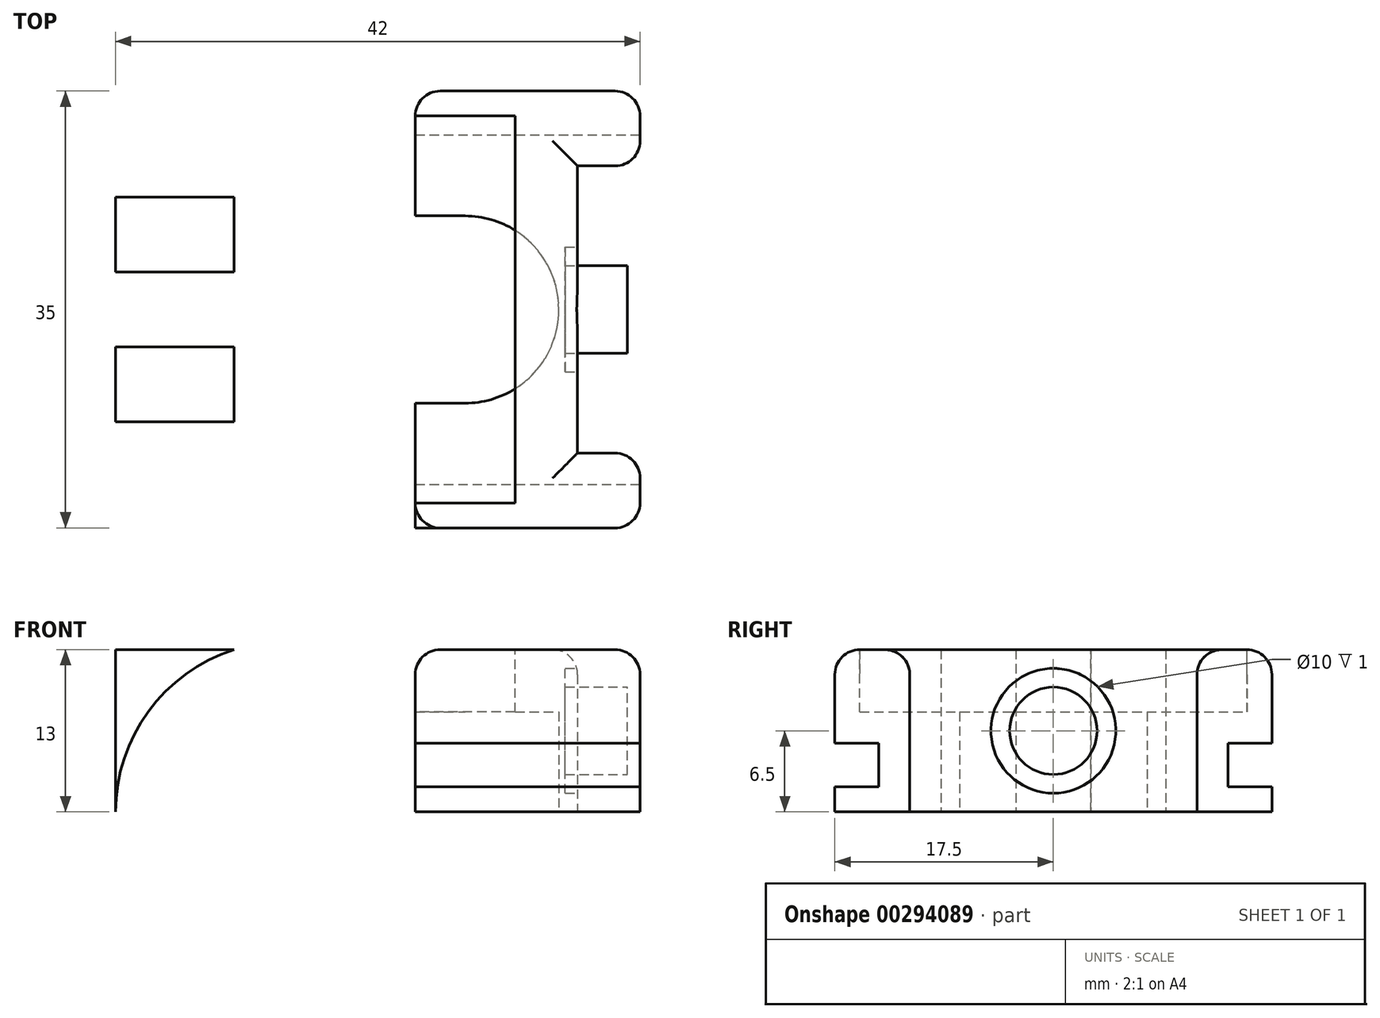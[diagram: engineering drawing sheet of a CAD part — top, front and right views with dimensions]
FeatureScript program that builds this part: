
annotation { "Feature Type Name" : "Feature", "Feature Type Description" : "" }
export const myFeature = defineFeature(function(context is Context, id is Id, definition is map)
    precondition{}
    {
        {
            var Q0;
            Q0=qCreatedBy(makeId("Top.planeOp"),FACE);
            var sketch = newSketch(context, id + "F0", { "sketchPlane" : qUnion([Q0])});
            skLineSegment(sketch, "E0", {"start": v(-15.8, 20.5) * mm, "end": v(2.2, 20.5) * mm});
            skLineSegment(sketch, "E1", {"start": v(2.2, 20.5) * mm, "end": v(2.2, 14.5) * mm});
            skLineSegment(sketch, "E2", {"start": v(2.2, 14.5) * mm, "end": v(-2.8, 14.5) * mm});
            skLineSegment(sketch, "E3", {"start": v(-2.8, 14.5) * mm, "end": v(-2.8, -8.5) * mm});
            skLineSegment(sketch, "E4", {"start": v(-2.8, -8.5) * mm, "end": v(2.2, -8.5) * mm});
            skPoint(sketch, "E4.endSnap0", {"position": v(2.2, 17.5) * mm});
            skLineSegment(sketch, "E5", {"start": v(2.2, -8.5) * mm, "end": v(2.2, -14.5) * mm});
            skLineSegment(sketch, "E6", {"start": v(2.2, -14.5) * mm, "end": v(-15.8, -14.5) * mm});
            skLineSegment(sketch, "E7", {"start": v(-15.8, -14.5) * mm, "end": v(-15.8, -6) * mm});
            skLineSegment(sketch, "E8", {"start": v(-15.8, 20.5) * mm, "end": v(-15.8, 12) * mm});
            skLineSegment(sketch, "E9", {"start": v(-15.8, 12) * mm, "end": v(-39.8, 12) * mm});
            skLineSegment(sketch, "E10", {"start": v(-15.8, -6) * mm, "end": v(-39.8, -6) * mm});
            skLineSegment(sketch, "E11", {"start": v(-39.8, -6) * mm, "end": v(-39.8, 0) * mm});
            skLineSegment(sketch, "E12", {"start": v(-39.8, 12) * mm, "end": v(-39.8, 6) * mm});
            skLineSegment(sketch, "E13", {"start": v(-39.8, 6) * mm, "end": v(-28.8, 6) * mm});
            skLineSegment(sketch, "E14", {"start": v(-28.8, 6) * mm, "end": v(-28.8, 0) * mm});
            skLineSegment(sketch, "E15", {"start": v(-28.8, 0) * mm, "end": v(-39.8, 0) * mm});
            skPoint(sketch, "E16.startSnap0", {"position": v(-28.8, 3) * mm});
            skLineSegment(sketch, "E17", {"start": v(-29.8, 12) * mm, "end": v(-29.8, -6) * mm});
            skSolve(sketch);
        }
        {
            var Q0;
            {var subQ0=sQuery(id+"F0.wireOp",EDGE,"E12");Q0=makeQuery(id+"F0.imprint","IMPRINT",FACE,{"disambiguationData":[TD([[makeQuery(id+"F0.imprint","IMPRINT",EDGE,{"derivedFrom":subQ0}),1.0]])]});}
            var Q1;
            {var subQ0=sQuery(id+"F0.wireOp",EDGE,"E11");Q1=makeQuery(id+"F0.imprint","IMPRINT",FACE,{"disambiguationData":[TD([[makeQuery(id+"F0.imprint","IMPRINT",EDGE,{"derivedFrom":subQ0}),-1.0]])]});}
            var Q2;
            Q2=makeQuery(id+"F0.imprint","IMPRINT",FACE,{"disambiguationData":[TD([[makeQuery(id+"F0.imprint","IMPRINT",EDGE,{"derivedFrom":sQuery(id+"F0.wireOp",EDGE,"E0")}),-1.0]])]});
            extrude(context, id + "F1", {"entities" : qUnion([Q0, Q1, Q2]), "depth" : 13 * mm});
        }
        {
            var Q0;
            Q0=makeQuery(id+"F1.opExtrude","SWEPT_FACE",FACE,{"disambiguationData":[OSD([sQuery(id+"F0.wireOp",EDGE,"E10")])]});
            var sketch = newSketch(context, id + "F2", { "sketchPlane" : qUnion([Q0])});
            skPoint(sketch, "E18", {"position": v(-26.15, 0) * mm});
            skArc(sketch, "E19", {"start": v(-39.8, 0) * mm, "mid": v(-37.18, 8.04) * mm, "end": v(-30.33, 13) * mm});
            skSolve(sketch);
        }
        {
            var Q0;
            {var subQ0=sQuery(id+"F2.wireOp",EDGE,"E19");Q0=makeQuery(id+"F2.imprint","IMPRINT",FACE,{"disambiguationData":[TD([[makeQuery(id+"F2.imprint","IMPRINT",EDGE,{"derivedFrom":subQ0}),1.0]])]});}
            extrude(context, id + "F3", {"entities" : qUnion([Q0]), "operationType" : NewBodyOperationType.REMOVE, "oppositeDirection" : true, "depth" : 25 * mm});
        }
        {
            var Q0;
            Q0=makeQuery(id+"F1.opExtrude","CAP_FACE",FACE,{"disambiguationData":[OSD([sQuery(id+"F0.wireOp",EDGE,"E0"),sQuery(id+"F0.wireOp",EDGE,"E1"),sQuery(id+"F0.wireOp",EDGE,"E2"),sQuery(id+"F0.wireOp",EDGE,"E3"),sQuery(id+"F0.wireOp",EDGE,"E4"),sQuery(id+"F0.wireOp",EDGE,"E5"),sQuery(id+"F0.wireOp",EDGE,"E6"),sQuery(id+"F0.wireOp",EDGE,"E7"),sQuery(id+"F0.wireOp",EDGE,"E8"),sQuery(id+"F0.wireOp",EDGE,"E9"),sQuery(id+"F0.wireOp",EDGE,"E10"),sQuery(id+"F0.wireOp",EDGE,"E11"),sQuery(id+"F0.wireOp",EDGE,"E12"),sQuery(id+"F0.wireOp",EDGE,"E13"),sQuery(id+"F0.wireOp",EDGE,"E14"),sQuery(id+"F0.wireOp",EDGE,"E15")])],"isStart":false});
            var sketch = newSketch(context, id + "F4", { "sketchPlane" : qUnion([Q0])});
            skLineSegment(sketch, "E20", {"start": v(-7.8, 18.5) * mm, "end": v(-30.33, 18.5) * mm});
            skLineSegment(sketch, "E21", {"start": v(-30.33, 18.5) * mm, "end": v(-30.33, -12.5) * mm});
            skLineSegment(sketch, "E22", {"start": v(-30.33, -12.5) * mm, "end": v(-7.8, -12.5) * mm});
            skLineSegment(sketch, "E23", {"start": v(-7.8, -12.5) * mm, "end": v(-7.8, 18.5) * mm});
            skSolve(sketch);
        }
        {
            var Q0;
            Q0 = qSketchRegion(id + "F4", true);
            extrude(context, id + "F5", {"entities" : qUnion([Q0]), "operationType" : NewBodyOperationType.REMOVE, "oppositeDirection" : true, "depth" : 5 * mm});
        }
        {
            var Q0;
            Q0=makeQuery(id+"F1.opExtrude","CAP_FACE",FACE,{"disambiguationData":[OSD([sQuery(id+"F0.wireOp",EDGE,"E0"),sQuery(id+"F0.wireOp",EDGE,"E1"),sQuery(id+"F0.wireOp",EDGE,"E2"),sQuery(id+"F0.wireOp",EDGE,"E3"),sQuery(id+"F0.wireOp",EDGE,"E4"),sQuery(id+"F0.wireOp",EDGE,"E5"),sQuery(id+"F0.wireOp",EDGE,"E6"),sQuery(id+"F0.wireOp",EDGE,"E7"),sQuery(id+"F0.wireOp",EDGE,"E8"),sQuery(id+"F0.wireOp",EDGE,"E9"),sQuery(id+"F0.wireOp",EDGE,"E10"),sQuery(id+"F0.wireOp",EDGE,"E11"),sQuery(id+"F0.wireOp",EDGE,"E12"),sQuery(id+"F0.wireOp",EDGE,"E13"),sQuery(id+"F0.wireOp",EDGE,"E14"),sQuery(id+"F0.wireOp",EDGE,"E15")])],"isStart":true});
            var sketch = newSketch(context, id + "F6", { "sketchPlane" : qUnion([Q0])});
            skLineSegment(sketch, "E24", {"start": v(-28.8, -3) * mm, "end": v(-2.8, -3) * mm, "construction": true});
            skLineSegment(sketch, "E25", {"start": v(-27.8, 4.5) * mm, "end": v(-3.53, 4.5) * mm, "construction": true});
            skPoint(sketch, "E26", {"position": v(-20.3, -3) * mm});
            skArc(sketch, "E27", {"start": v(-20.3, 4.5) * mm, "mid": v(-27.8, -3) * mm, "end": v(-20.3, -10.5) * mm});
            skPoint(sketch, "E28", {"position": v(-11.8, -3) * mm});
            skArc(sketch, "E29", {"start": v(-11.8, 4.5) * mm, "mid": v(-4.3, -3) * mm, "end": v(-11.8, -10.5) * mm});
            skLineSegment(sketch, "E30", {"start": v(-20.3, 4.5) * mm, "end": v(-11.8, 4.5) * mm});
            skLineSegment(sketch, "E31", {"start": v(-20.3, -10.5) * mm, "end": v(-11.8, -10.5) * mm});
            skSolve(sketch);
        }
        {
            var Q0;
            Q0 = qSketchRegion(id + "F6", true);
            var Q1;
            Q1=makeQuery(id+"F5.boolean.opBoolean","COPY",FACE,{"derivedFrom":makeQuery(id+"F5.opExtrude","CAP_FACE",FACE,{"disambiguationData":[OSD([sQuery(id+"F4.wireOp",EDGE,"E20"),sQuery(id+"F4.wireOp",EDGE,"E21"),sQuery(id+"F4.wireOp",EDGE,"E22"),sQuery(id+"F4.wireOp",EDGE,"E23")])],"isStart":false})});
            extrude(context, id + "F7", {"entities" : qUnion([Q0]), "operationType" : NewBodyOperationType.REMOVE, "endBound" : BoundingType.UP_TO_SURFACE, "oppositeDirection" : true, "endBoundEntityFace" : qUnion([Q1]), "depth" : 25 * mm});
        }
        {
            var Q0;
            Q0=makeQuery(id+"F1.opExtrude","SWEPT_FACE",FACE,{"disambiguationData":[OSD([sQuery(id+"F0.wireOp",EDGE,"E3")])]});
            var sketch = newSketch(context, id + "F8", { "sketchPlane" : qUnion([Q0])});
            skPoint(sketch, "E32", {"position": v(3, 6.5) * mm});
            skPoint(sketch, "E32.positionSnap0", {"position": v(3, 0) * mm});
            skPoint(sketch, "E32.positionSnap1", {"position": v(14.5, 6.5) * mm});
            skCircle(sketch, "E33", {"center": v(3, 6.5) * mm, "radius": 5 * mm});
            skCircle(sketch, "E34", {"center": v(3, 6.5) * mm, "radius": 3.5 * mm});
            skSolve(sketch);
        }
        {
            var Q0;
            Q0=makeQuery(id+"F8.imprint","IMPRINT",FACE,{"disambiguationData":[TD([[makeQuery(id+"F8.imprint","IMPRINT",EDGE,{"derivedFrom":sQuery(id+"F8.wireOp",EDGE,"E33")}),1.0]])]});
            extrude(context, id + "F9", {"entities" : qUnion([Q0]), "operationType" : NewBodyOperationType.REMOVE, "oppositeDirection" : true, "depth" : 1 * mm});
        }
        {
            var Q0;
            Q0=makeQuery(id+"F9.boolean.opBoolean","SPLIT",FACE,{"disambiguationData":[TD([makeQuery(id+"F9.opExtrude","SWEPT_FACE",FACE,{"disambiguationData":[OSD([sQuery(id+"F8.wireOp",EDGE,"E34")])]})])],"derivedFrom":makeQuery(id+"F1.opExtrude","SWEPT_FACE",FACE,{"disambiguationData":[OSD([sQuery(id+"F0.wireOp",EDGE,"E3")])]})});
            extrude(context, id + "F10", {"entities" : qUnion([Q0]), "operationType" : NewBodyOperationType.ADD, "depth" : 4 * mm});
        }
        {
            var Q0;
            Q0=makeQuery(id+"F1.opExtrude","SWEPT_FACE",FACE,{"disambiguationData":[OSD([sQuery(id+"F0.wireOp",EDGE,"E5")])]});
            var sketch = newSketch(context, id + "F11", { "sketchPlane" : qUnion([Q0])});
            skLineSegment(sketch, "E35", {"start": v(-14.5, 2) * mm, "end": v(-11, 2) * mm});
            skLineSegment(sketch, "E36", {"start": v(-11, 2) * mm, "end": v(-11, 5.5) * mm});
            skLineSegment(sketch, "E37", {"start": v(-11, 5.5) * mm, "end": v(-14.5, 5.5) * mm});
            skLineSegment(sketch, "E38", {"start": v(-14.5, 5.5) * mm, "end": v(-14.5, 2) * mm});
            skSolve(sketch);
        }
        {
            var Q0;
            Q0=makeQuery(id+"F11.imprint","IMPRINT",FACE,{"disambiguationData":[TD([[makeQuery(id+"F11.imprint","IMPRINT",EDGE,{"derivedFrom":sQuery(id+"F11.wireOp",EDGE,"E35")}),1.0]])]});
            extrude(context, id + "F12", {"entities" : qUnion([Q0]), "operationType" : NewBodyOperationType.REMOVE, "endBound" : BoundingType.THROUGH_ALL, "oppositeDirection" : true, "depth" : 25 * mm});
        }
        {
            var Q0;
            Q0=makeQuery(id+"F1.opExtrude","SWEPT_FACE",FACE,{"disambiguationData":[OSD([sQuery(id+"F0.wireOp",EDGE,"E1")])]});
            var sketch = newSketch(context, id + "F13", { "sketchPlane" : qUnion([Q0])});
            skLineSegment(sketch, "E39", {"start": v(20.5, 2) * mm, "end": v(17, 2) * mm});
            skLineSegment(sketch, "E40", {"start": v(17, 2) * mm, "end": v(17, 5.5) * mm});
            skLineSegment(sketch, "E41", {"start": v(17, 5.5) * mm, "end": v(20.5, 5.5) * mm});
            skLineSegment(sketch, "E42", {"start": v(20.5, 5.5) * mm, "end": v(20.5, 2) * mm});
            skSolve(sketch);
        }
        {
            var Q0;
            Q0=makeQuery(id+"F13.imprint","IMPRINT",FACE,{"disambiguationData":[TD([[makeQuery(id+"F13.imprint","IMPRINT",EDGE,{"derivedFrom":sQuery(id+"F13.wireOp",EDGE,"E39")}),-1.0]])]});
            extrude(context, id + "F14", {"entities" : qUnion([Q0]), "operationType" : NewBodyOperationType.REMOVE, "endBound" : BoundingType.THROUGH_ALL, "oppositeDirection" : true, "depth" : 25 * mm});
        }
        {
            var Q0;
            Q0=makeQuery(id+"F1.opExtrude","CAP_EDGE",EDGE,{"disambiguationData":[OSD([sQuery(id+"F0.wireOp",EDGE,"E6")])],"isStart":false});
            var Q1;
            Q1=makeQuery(id+"F1.opExtrude","CAP_EDGE",EDGE,{"disambiguationData":[OSD([sQuery(id+"F0.wireOp",EDGE,"E5")])],"isStart":false});
            var Q2;
            Q2=makeQuery(id+"F1.opExtrude","CAP_EDGE",EDGE,{"disambiguationData":[OSD([sQuery(id+"F0.wireOp",EDGE,"E4")])],"isStart":false});
            var Q3;
            Q3=makeQuery(id+"F1.opExtrude","CAP_EDGE",EDGE,{"disambiguationData":[OSD([sQuery(id+"F0.wireOp",EDGE,"E3")])],"isStart":false});
            var Q4;
            Q4=makeQuery(id+"F1.opExtrude","CAP_EDGE",EDGE,{"disambiguationData":[OSD([sQuery(id+"F0.wireOp",EDGE,"E2")])],"isStart":false});
            var Q5;
            Q5=makeQuery(id+"F1.opExtrude","CAP_EDGE",EDGE,{"disambiguationData":[OSD([sQuery(id+"F0.wireOp",EDGE,"E0")])],"isStart":false});
            var Q6;
            Q6=makeQuery(id+"F1.opExtrude","CAP_EDGE",EDGE,{"disambiguationData":[OSD([sQuery(id+"F0.wireOp",EDGE,"E1")])],"isStart":false});
            var Q7;
            {var subQ0=sQuery(id+"F0.wireOp",EDGE,"E0");var subQ1=sQuery(id+"F0.wireOp",EDGE,"E1");Q7=makeQuery(id+"F14.boolean.opBoolean","SPLIT",EDGE,{"disambiguationData":[TD([makeQuery(id+"F14.opExtrude","SWEPT_FACE",FACE,{"disambiguationData":[OSD([sQuery(id+"F13.wireOp",EDGE,"E41")])]})])],"derivedFrom":makeQuery(id+"F1.opExtrude","SWEPT_EDGE",EDGE,{"disambiguationData":[OSD([subQ0,subQ1])]})});}
            var Q8;
            {var subQ0=sQuery(id+"F0.wireOp",EDGE,"E0");var subQ1=sQuery(id+"F0.wireOp",EDGE,"E8");Q8=makeQuery(id+"F14.boolean.opBoolean","SPLIT",EDGE,{"disambiguationData":[TD([makeQuery(id+"F14.opExtrude","SWEPT_FACE",FACE,{"disambiguationData":[OSD([sQuery(id+"F13.wireOp",EDGE,"E41")])]})])],"derivedFrom":makeQuery(id+"F1.opExtrude","SWEPT_EDGE",EDGE,{"disambiguationData":[OSD([subQ0,subQ1])]})});}
            var Q9;
            {var subQ0=sQuery(id+"F0.wireOp",EDGE,"E0");var subQ1=sQuery(id+"F0.wireOp",EDGE,"E8");Q9=makeQuery(id+"F14.boolean.opBoolean","SPLIT",EDGE,{"disambiguationData":[TD([makeQuery(id+"F14.opExtrude","SWEPT_FACE",FACE,{"disambiguationData":[OSD([sQuery(id+"F13.wireOp",EDGE,"E39")])]})])],"derivedFrom":makeQuery(id+"F1.opExtrude","SWEPT_EDGE",EDGE,{"disambiguationData":[OSD([subQ0,subQ1])]})});}
            var Q10;
            {var subQ0=sQuery(id+"F0.wireOp",EDGE,"E6");var subQ1=sQuery(id+"F0.wireOp",EDGE,"E5");Q10=makeQuery(id+"F12.boolean.opBoolean","SPLIT",EDGE,{"disambiguationData":[TD([makeQuery(id+"F12.opExtrude","SWEPT_FACE",FACE,{"disambiguationData":[OSD([sQuery(id+"F11.wireOp",EDGE,"E37")])]})])],"derivedFrom":makeQuery(id+"F1.opExtrude","SWEPT_EDGE",EDGE,{"disambiguationData":[OSD([subQ1,subQ0])]})});}
            var Q11;
            Q11=makeQuery(id+"F1.opExtrude","SWEPT_EDGE",EDGE,{"disambiguationData":[OSD([sQuery(id+"F0.wireOp",EDGE,"E4"),sQuery(id+"F0.wireOp",EDGE,"E5")])]});
            var Q12;
            Q12=makeQuery(id+"F1.opExtrude","SWEPT_EDGE",EDGE,{"disambiguationData":[OSD([sQuery(id+"F0.wireOp",EDGE,"E1"),sQuery(id+"F0.wireOp",EDGE,"E2")])]});
            var Q13;
            {var subQ0=sQuery(id+"F0.wireOp",EDGE,"E6");var subQ1=sQuery(id+"F0.wireOp",EDGE,"E5");Q13=makeQuery(id+"F12.boolean.opBoolean","SPLIT",EDGE,{"disambiguationData":[TD([makeQuery(id+"F12.opExtrude","SWEPT_FACE",FACE,{"disambiguationData":[OSD([sQuery(id+"F11.wireOp",EDGE,"E35")])]})])],"derivedFrom":makeQuery(id+"F1.opExtrude","SWEPT_EDGE",EDGE,{"disambiguationData":[OSD([subQ1,subQ0])]})});}
            var Q14;
            {var subQ0=sQuery(id+"F0.wireOp",EDGE,"E0");var subQ1=sQuery(id+"F0.wireOp",EDGE,"E1");Q14=makeQuery(id+"F14.boolean.opBoolean","SPLIT",EDGE,{"disambiguationData":[TD([makeQuery(id+"F14.opExtrude","SWEPT_FACE",FACE,{"disambiguationData":[OSD([sQuery(id+"F13.wireOp",EDGE,"E39")])]})])],"derivedFrom":makeQuery(id+"F1.opExtrude","SWEPT_EDGE",EDGE,{"disambiguationData":[OSD([subQ0,subQ1])]})});}
            var Q15;
            {var subQ0=sQuery(id+"F0.wireOp",EDGE,"E7");var subQ1=sQuery(id+"F0.wireOp",EDGE,"E6");Q15=makeQuery(id+"F12.boolean.opBoolean","SPLIT",EDGE,{"disambiguationData":[TD([makeQuery(id+"F12.opExtrude","SWEPT_FACE",FACE,{"disambiguationData":[OSD([sQuery(id+"F11.wireOp",EDGE,"E37")])]})])],"derivedFrom":makeQuery(id+"F1.opExtrude","SWEPT_EDGE",EDGE,{"disambiguationData":[OSD([subQ1,subQ0])]})});}
            var Q16;
            Q16=makeQuery(id+"F1.opExtrude","CAP_EDGE",EDGE,{"disambiguationData":[OSD([sQuery(id+"F0.wireOp",EDGE,"E7")])],"isStart":false});
            var Q17;
            Q17=makeQuery(id+"F1.opExtrude","CAP_EDGE",EDGE,{"disambiguationData":[OSD([sQuery(id+"F0.wireOp",EDGE,"E8")])],"isStart":false});
            fillet(context, id + "F15", {"entities" : qUnion([Q0, Q1, Q2, Q3, Q4, Q5, Q6, Q7, Q8, Q9, Q10, Q11, Q12, Q13, Q14, Q15, Q16, Q17]), "radius" : 2 * mm, "tangentPropagation" : true, "allowEdgeOverflow" : false});
        }
    });
